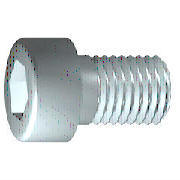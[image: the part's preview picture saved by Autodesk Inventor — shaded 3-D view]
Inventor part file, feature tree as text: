
AUTODESK INVENTOR PART (.ipt)
format: ipt  version: 2020 (Build 240168000, 168)  size: 190,464 bytes
history: native  units: mm (DEFAULTED — no unit token found)
features: sketch x2, extrude x1, plane x1, fillet x1
ambient origin geometry x7: Origin, YZ Plane, XY Plane, X Axis, Y Axis, Z Axis, Center Point
bodies: Solid1 (feature_tree), Body (feature_tree)
feature tree (5):
  extrude  "Slot"  Depth=2.0mm
  plane  "Work Plane1"
  fillet  "Fillet2"  Radius=2.0mm
  sketch  "Sketch1"  dims[d1=12.0mm d2=0.306825mm d3=2.0mm]
  sketch  "Sketch2"  dims[d4=1.5mm d5=60.0deg d6=3.0mm d7=3.0mm d8=2.309401mm d9=5.5mm d10=90.0deg d11=10.0mm d12=0.0mm d13=12.0mm d14=0.0mm d15=0.306725mm d16=0.306725mm d17=0.3mm d19=0.0mm d26=20.0mm d27=45.0deg d28=0.0mm d29=0.0mm d30=0.1mm]
